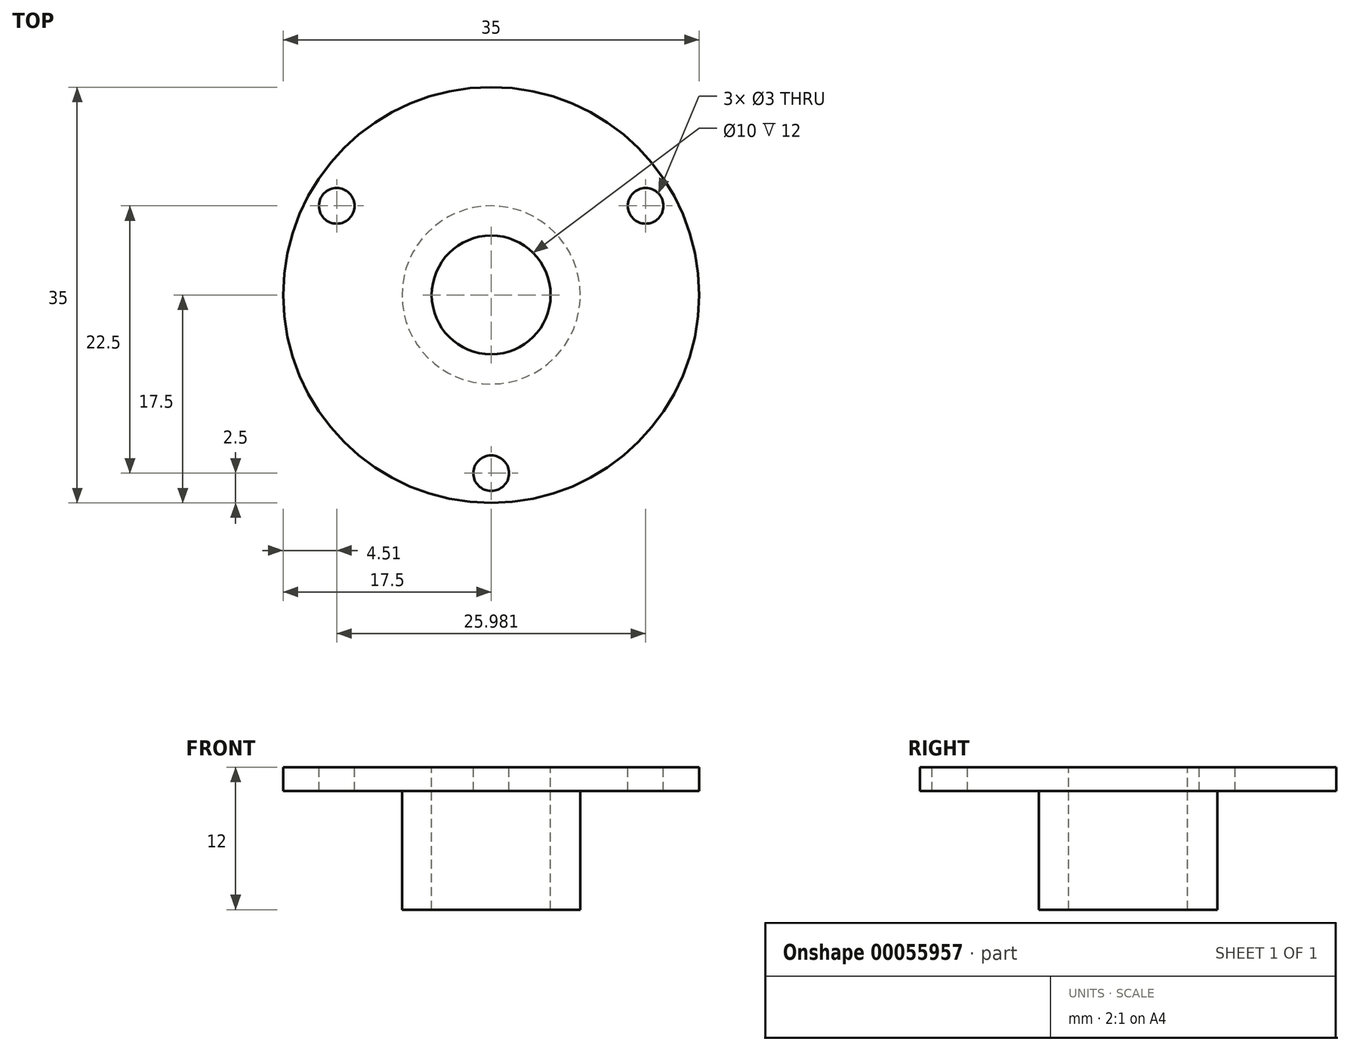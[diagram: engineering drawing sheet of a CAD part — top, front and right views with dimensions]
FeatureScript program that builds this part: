
annotation { "Feature Type Name" : "Feature", "Feature Type Description" : "" }
export const myFeature = defineFeature(function(context is Context, id is Id, definition is map)
    precondition{}
    {
        {
            var Q0;
            Q0=qCreatedBy(makeId("Top.planeOp"),FACE);
            var sketch = newSketch(context, id + "F0", { "sketchPlane" : qUnion([Q0])});
            skCircle(sketch, "E0", {"center": v(0, 0) * mm, "radius": 17.5 * mm});
            skCircle(sketch, "E1", {"center": v(0, 0) * mm, "radius": 5 * mm});
            skSolve(sketch);
        }
        {
            var Q0;
            Q0=makeQuery(id+"F0.imprint","IMPRINT",FACE,{"disambiguationData":[TD([[makeQuery(id+"F0.imprint","IMPRINT",EDGE,{"derivedFrom":sQuery(id+"F0.wireOp",EDGE,"E0")}),1.0]])]});
            extrude(context, id + "F1", {"entities" : qUnion([Q0]), "oppositeDirection" : true, "depth" : 2 * mm});
        }
        {
            var Q0;
            Q0=makeQuery(id+"F1.opExtrude","CAP_FACE",FACE,{"disambiguationData":[OSD([sQuery(id+"F0.wireOp",EDGE,"E0"),sQuery(id+"F0.wireOp",EDGE,"E1")])],"isStart":false});
            var sketch = newSketch(context, id + "F2", { "sketchPlane" : qUnion([Q0])});
            skCircle(sketch, "E2", {"center": v(0, 0) * mm, "radius": 7.5 * mm});
            skSolve(sketch);
        }
        {
            var Q0;
            Q0=makeQuery(id+"F2.imprint","IMPRINT",FACE,{"disambiguationData":[TD([[makeQuery(id+"F2.imprint","IMPRINT",EDGE,{"derivedFrom":sQuery(id+"F2.wireOp",EDGE,"E2")}),1.0]])]});
            extrude(context, id + "F3", {"entities" : qUnion([Q0]), "operationType" : NewBodyOperationType.ADD, "depth" : 10 * mm});
        }
        {
            var Q0;
            Q0=makeQuery(id+"F1.opExtrude","CAP_FACE",FACE,{"disambiguationData":[OSD([sQuery(id+"F0.wireOp",EDGE,"E0"),sQuery(id+"F0.wireOp",EDGE,"E1")])],"isStart":true});
            var sketch = newSketch(context, id + "F4", { "sketchPlane" : qUnion([Q0])});
            skCircle(sketch, "E3.cCircle", {"center": v(0, 0) * mm, "radius": 7.5 * mm, "construction": true});
            skLineSegment(sketch, "E3.0", {"start": v(-13, 7.5) * mm, "end": v(13, 7.5) * mm, "construction": true});
            skLineSegment(sketch, "E3.1", {"start": v(13, 7.5) * mm, "end": v(0, -15) * mm, "construction": true});
            skLineSegment(sketch, "E3.2", {"start": v(0, -15) * mm, "end": v(-13, 7.5) * mm, "construction": true});
            skPoint(sketch, "E3.0.midPoint", {"position": v(0, 7.5) * mm});
            skCircle(sketch, "E4", {"center": v(-13, 7.5) * mm, "radius": 1.5 * mm});
            skCircle(sketch, "E5", {"center": v(13, 7.5) * mm, "radius": 1.5 * mm});
            skCircle(sketch, "E6", {"center": v(0, -15) * mm, "radius": 1.5 * mm});
            skSolve(sketch);
        }
        {
            var Q0;
            Q0=makeQuery(id+"F4.imprint","IMPRINT",FACE,{"disambiguationData":[TD([[makeQuery(id+"F4.imprint","IMPRINT",EDGE,{"derivedFrom":sQuery(id+"F4.wireOp",EDGE,"E4")}),1.0]])]});
            var Q1;
            Q1=makeQuery(id+"F4.imprint","IMPRINT",FACE,{"disambiguationData":[TD([[makeQuery(id+"F4.imprint","IMPRINT",EDGE,{"derivedFrom":sQuery(id+"F4.wireOp",EDGE,"E5")}),1.0]])]});
            var Q2;
            Q2=makeQuery(id+"F4.imprint","IMPRINT",FACE,{"disambiguationData":[TD([[makeQuery(id+"F4.imprint","IMPRINT",EDGE,{"derivedFrom":sQuery(id+"F4.wireOp",EDGE,"E6")}),1.0]])]});
            extrude(context, id + "F5", {"entities" : qUnion([Q0, Q1, Q2]), "operationType" : NewBodyOperationType.REMOVE, "endBound" : BoundingType.UP_TO_NEXT, "oppositeDirection" : true, "depth" : 25 * mm});
        }
    });
